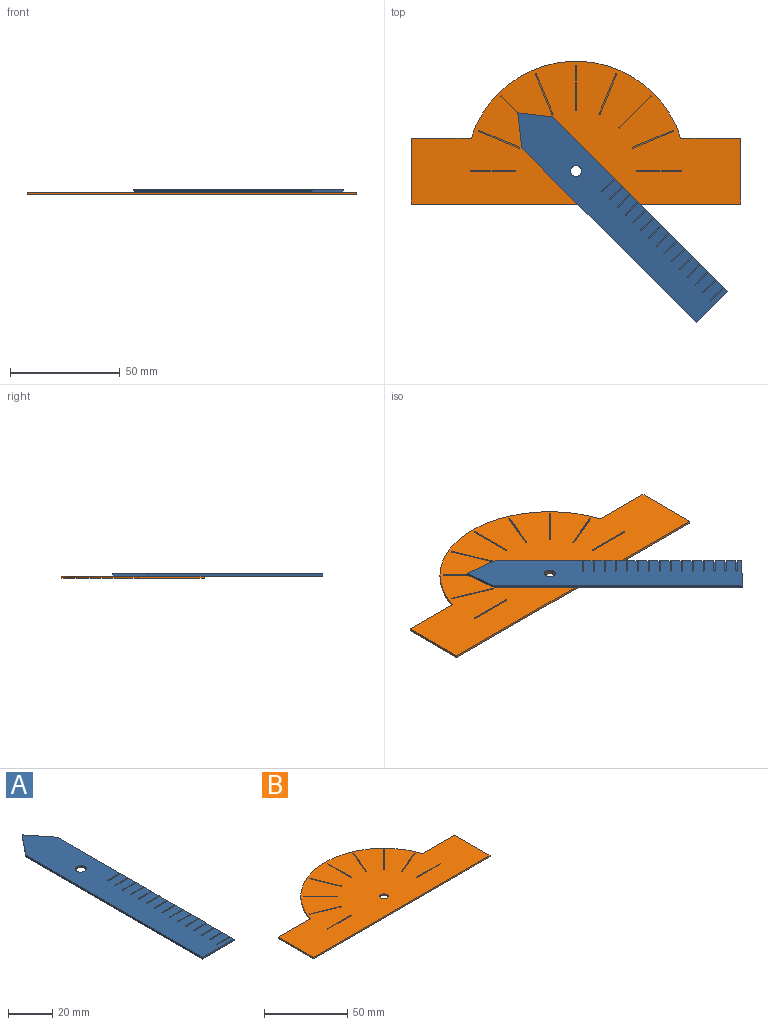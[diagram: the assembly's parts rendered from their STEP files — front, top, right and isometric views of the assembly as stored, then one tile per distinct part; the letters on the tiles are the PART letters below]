
ASSEMBLY  parts=2 mates=1
PART A: 68 faces, bbox 20x125x1 mm
  f0: plane 112.42x1mm, normal (1,0,0), area 108.7mm2, adj f1,f2,f5,f6,f8,f10,f11,f12
  f1: plane 125x20mm, normal (0,0,1), area 2293.1mm2, adj f0,f2,f3,f4,f5,f7,f8,f9
  f2: plane 12.58x10mm, normal (0.78,0.62,0), area 16.1mm2, adj f0,f1,f3,f6
  f3: plane 12.58x10mm, normal (-0.78,0.62,0), area 16.1mm2, adj f1,f2,f4,f6
  f4: plane 112.42x1mm, normal (-1,0,0), area 112.4mm2, adj f1,f3,f5,f6
  f5: plane 20x1mm, normal (0,-1,0), area 20mm2, adj f0,f1,f4,f6
  f6: plane 125x20mm, normal (0,0,-1), area 2354.5mm2, adj f0,f2,f3,f4,f5,f7
  f7: cylinder r=2.5mm len=5mm, axis (0,0,1), area 15.7mm2, adj f1,f6
  f8: plane 8x0.5mm, normal (0,-1,0), area 4mm2, adj f0,f1,f9,f11
  f9: cylinder r=0.25mm len=0.5mm, axis (0,0,1), area 0.4mm2, adj f1,f8,f10,f11
  f10: plane 8x0.5mm, normal (0,1,0), area 4mm2, adj f0,f1,f9,f11
  f11: plane 8.25x0.5mm, normal (0,0,1), area 4.1mm2, adj f0,f8,f9,f10
  f12: plane 8x0.5mm, normal (0,-1,0), area 4mm2, adj f0,f1,f13,f15
  f13: cylinder r=0.25mm len=0.5mm, axis (0,0,1), area 0.4mm2, adj f1,f12,f14,f15
  f14: plane 8x0.5mm, normal (0,1,0), area 4mm2, adj f0,f1,f13,f15
  f15: plane 8.25x0.5mm, normal (0,0,1), area 4.1mm2, adj f0,f12,f13,f14
  f16: plane 8x0.5mm, normal (0,-1,0), area 4mm2, adj f0,f1,f17,f19
  f17: cylinder r=0.25mm len=0.5mm, axis (0,0,1), area 0.4mm2, adj f1,f16,f18,f19
  f18: plane 8x0.5mm, normal (0,1,0), area 4mm2, adj f0,f1,f17,f19
  f19: plane 8.25x0.5mm, normal (0,0,1), area 4.1mm2, adj f0,f16,f17,f18
  f20: plane 8x0.5mm, normal (0,-1,0), area 4mm2, adj f0,f1,f21,f23
  f21: cylinder r=0.25mm len=0.5mm, axis (0,0,1), area 0.4mm2, adj f1,f20,f22,f23
  f22: plane 8x0.5mm, normal (0,1,0), area 4mm2, adj f0,f1,f21,f23
  f23: plane 8.25x0.5mm, normal (0,0,1), area 4.1mm2, adj f0,f20,f21,f22
  f24: plane 8x0.5mm, normal (0,-1,0), area 4mm2, adj f0,f1,f25,f27
  f25: cylinder r=0.25mm len=0.5mm, axis (0,0,1), area 0.4mm2, adj f1,f24,f26,f27
  f26: plane 8x0.5mm, normal (0,1,0), area 4mm2, adj f0,f1,f25,f27
  f27: plane 8.25x0.5mm, normal (0,0,1), area 4.1mm2, adj f0,f24,f25,f26
  f28: plane 8x0.5mm, normal (0,-1,0), area 4mm2, adj f0,f1,f29,f31
  f29: cylinder r=0.25mm len=0.5mm, axis (0,0,1), area 0.4mm2, adj f1,f28,f30,f31
  f30: plane 8x0.5mm, normal (0,1,0), area 4mm2, adj f0,f1,f29,f31
  f31: plane 8.25x0.5mm, normal (0,0,1), area 4.1mm2, adj f0,f28,f29,f30
  f32: plane 8x0.5mm, normal (0,-1,0), area 4mm2, adj f0,f1,f33,f35
  f33: cylinder r=0.25mm len=0.5mm, axis (0,0,1), area 0.4mm2, adj f1,f32,f34,f35
  f34: plane 8x0.5mm, normal (0,1,0), area 4mm2, adj f0,f1,f33,f35
  f35: plane 8.25x0.5mm, normal (0,0,1), area 4.1mm2, adj f0,f32,f33,f34
  f36: plane 8x0.5mm, normal (0,-1,0), area 4mm2, adj f0,f1,f37,f39
  f37: cylinder r=0.25mm len=0.5mm, axis (0,0,1), area 0.4mm2, adj f1,f36,f38,f39
  f38: plane 8x0.5mm, normal (0,1,0), area 4mm2, adj f0,f1,f37,f39
  f39: plane 8.25x0.5mm, normal (0,0,1), area 4.1mm2, adj f0,f36,f37,f38
  f40: plane 8x0.5mm, normal (0,-1,0), area 4mm2, adj f0,f1,f41,f43
  f41: cylinder r=0.25mm len=0.5mm, axis (0,0,1), area 0.4mm2, adj f1,f40,f42,f43
  f42: plane 8x0.5mm, normal (0,1,0), area 4mm2, adj f0,f1,f41,f43
  f43: plane 8.25x0.5mm, normal (0,0,1), area 4.1mm2, adj f0,f40,f41,f42
  f44: plane 8x0.5mm, normal (0,-1,0), area 4mm2, adj f0,f1,f45,f47
  f45: cylinder r=0.25mm len=0.5mm, axis (0,0,1), area 0.4mm2, adj f1,f44,f46,f47
  f46: plane 8x0.5mm, normal (0,1,0), area 4mm2, adj f0,f1,f45,f47
  f47: plane 8.25x0.5mm, normal (0,0,1), area 4.1mm2, adj f0,f44,f45,f46
  f48: plane 8x0.5mm, normal (0,-1,0), area 4mm2, adj f0,f1,f49,f51
  f49: cylinder r=0.25mm len=0.5mm, axis (0,0,1), area 0.4mm2, adj f1,f48,f50,f51
  f50: plane 8x0.5mm, normal (0,1,0), area 4mm2, adj f0,f1,f49,f51
  f51: plane 8.25x0.5mm, normal (0,0,1), area 4.1mm2, adj f0,f48,f49,f50
  f52: plane 8x0.5mm, normal (0,-1,0), area 4mm2, adj f0,f1,f53,f55
  f53: cylinder r=0.25mm len=0.5mm, axis (0,0,1), area 0.4mm2, adj f1,f52,f54,f55
  f54: plane 8x0.5mm, normal (0,1,0), area 4mm2, adj f0,f1,f53,f55
  f55: plane 8.25x0.5mm, normal (0,0,1), area 4.1mm2, adj f0,f52,f53,f54
  f56: plane 8x0.5mm, normal (0,-1,0), area 4mm2, adj f0,f1,f57,f59
  f57: cylinder r=0.25mm len=0.5mm, axis (0,0,1), area 0.4mm2, adj f1,f56,f58,f59
  f58: plane 8x0.5mm, normal (0,1,0), area 4mm2, adj f0,f1,f57,f59
  f59: plane 8.25x0.5mm, normal (0,0,1), area 4.1mm2, adj f0,f56,f57,f58
  f60: plane 8x0.5mm, normal (0,-1,0), area 4mm2, adj f0,f1,f61,f63
  f61: cylinder r=0.25mm len=0.5mm, axis (0,0,1), area 0.4mm2, adj f1,f60,f62,f63
  f62: plane 8x0.5mm, normal (0,1,0), area 4mm2, adj f0,f1,f61,f63
  f63: plane 8.25x0.5mm, normal (0,0,1), area 4.1mm2, adj f0,f60,f61,f62
  f64: plane 8x0.5mm, normal (0,1,0), area 4mm2, adj f0,f1,f66,f67
  f65: plane 8x0.5mm, normal (0,-1,0), area 4mm2, adj f0,f1,f66,f67
  f66: cylinder r=0.25mm len=0.5mm, axis (0,0,1), area 0.4mm2, adj f1,f64,f65,f67
  f67: plane 8.25x0.5mm, normal (0,0,1), area 4.1mm2, adj f0,f64,f65,f66
PART B: 54 faces, bbox 150x65x1 mm
  f0: plane 27.3x1mm, normal (0,1,0), area 27.3mm2, adj f1,f5,f6,f7
  f1: plane 30x1mm, normal (-1,0,0), area 30mm2, adj f0,f2,f6,f7
  f2: plane 150x1mm, normal (0,-1,0), area 150mm2, adj f1,f3,f6,f7
  f3: plane 30x1mm, normal (1,0,0), area 30mm2, adj f2,f4,f6,f7
  f4: plane 27.3x1mm, normal (0,1,0), area 27.3mm2, adj f3,f5,f6,f7
  f5: cylinder r=50mm len=95.39mm, axis (0,0,1), area 126.6mm2, adj f0,f4,f6,f7
  f6: plane 150x65mm, normal (0,0,-1), area 6930.2mm2, adj f0,f1,f2,f3,f4,f5,f8
  f7: plane 150x65mm, normal (0,0,1), area 6838.4mm2, adj f0,f1,f2,f3,f4,f5,f8,f9
  f8: cylinder r=2.5mm len=5mm, axis (0,0,1), area 15.7mm2, adj f6,f7
  f9: plane 20x0.5mm, normal (0,1,0), area 10mm2, adj f7,f10,f12,f13
  f10: cylinder r=0.25mm len=0.5mm, axis (0,0,1), area 0.4mm2, adj f7,f9,f11,f13
  f11: plane 20x0.5mm, normal (0,-1,0), area 10mm2, adj f7,f10,f12,f13
  f12: cylinder r=0.25mm len=0.5mm, axis (0,0,1), area 0.4mm2, adj f7,f9,f11,f13
  f13: plane 20.5x0.5mm, normal (0,0,1), area 10.2mm2, adj f9,f10,f11,f12
  f14: plane 18.48x7.65mm, normal (-0.38,0.92,0), area 10mm2, adj f7,f15,f17,f18
  f15: cylinder r=0.25mm len=0.5mm, axis (0,0,1), area 0.4mm2, adj f7,f14,f16,f18
  f16: plane 18.48x7.65mm, normal (0.38,-0.92,0), area 10mm2, adj f7,f15,f17,f18
  f17: cylinder r=0.25mm len=0.5mm, axis (0,0,1), area 0.4mm2, adj f7,f14,f16,f18
  f18: plane 18.98x8.15mm, normal (0,0,1), area 10.2mm2, adj f14,f15,f16,f17
  f19: plane 14.14x14.14mm, normal (-0.71,0.71,0), area 10mm2, adj f7,f20,f22,f23
  f20: cylinder r=0.25mm len=0.5mm, axis (0,0,1), area 0.4mm2, adj f7,f19,f21,f23
  f21: plane 14.14x14.14mm, normal (0.71,-0.71,0), area 10mm2, adj f7,f20,f22,f23
  f22: cylinder r=0.25mm len=0.5mm, axis (0,0,1), area 0.4mm2, adj f7,f19,f21,f23
  f23: plane 14.64x14.64mm, normal (0,0,1), area 10.2mm2, adj f19,f20,f21,f22
  f24: plane 18.48x7.65mm, normal (-0.92,0.38,0), area 10mm2, adj f7,f25,f27,f28
  f25: cylinder r=0.25mm len=0.5mm, axis (0,0,1), area 0.4mm2, adj f7,f24,f26,f28
  f26: plane 18.48x7.65mm, normal (0.92,-0.38,0), area 10mm2, adj f7,f25,f27,f28
  f27: cylinder r=0.25mm len=0.5mm, axis (0,0,1), area 0.4mm2, adj f7,f24,f26,f28
  f28: plane 18.98x8.15mm, normal (0,0,1), area 10.2mm2, adj f24,f25,f26,f27
  f29: plane 20x0.5mm, normal (-1,0,0), area 10mm2, adj f7,f30,f32,f33
  f30: cylinder r=0.25mm len=0.5mm, axis (0,0,1), area 0.4mm2, adj f7,f29,f31,f33
  f31: plane 20x0.5mm, normal (1,0,0), area 10mm2, adj f7,f30,f32,f33
  f32: cylinder r=0.25mm len=0.5mm, axis (0,0,1), area 0.4mm2, adj f7,f29,f31,f33
  f33: plane 20.5x0.5mm, normal (0,0,1), area 10.2mm2, adj f29,f30,f31,f32
  f34: plane 18.48x7.65mm, normal (-0.92,-0.38,0), area 10mm2, adj f7,f35,f37,f38
  f35: cylinder r=0.25mm len=0.5mm, axis (0,0,1), area 0.4mm2, adj f7,f34,f36,f38
  f36: plane 18.48x7.65mm, normal (0.92,0.38,0), area 10mm2, adj f7,f35,f37,f38
  f37: cylinder r=0.25mm len=0.5mm, axis (0,0,1), area 0.4mm2, adj f7,f34,f36,f38
  f38: plane 18.98x8.15mm, normal (0,0,1), area 10.2mm2, adj f34,f35,f36,f37
  f39: plane 14.14x14.14mm, normal (-0.71,-0.71,0), area 10mm2, adj f7,f40,f42,f43
  f40: cylinder r=0.25mm len=0.5mm, axis (0,0,1), area 0.4mm2, adj f7,f39,f41,f43
  f41: plane 14.14x14.14mm, normal (0.71,0.71,0), area 10mm2, adj f7,f40,f42,f43
  f42: cylinder r=0.25mm len=0.5mm, axis (0,0,1), area 0.4mm2, adj f7,f39,f41,f43
  f43: plane 14.64x14.64mm, normal (0,0,1), area 10.2mm2, adj f39,f40,f41,f42
  f44: plane 18.48x7.65mm, normal (-0.38,-0.92,0), area 10mm2, adj f7,f45,f47,f48
  f45: cylinder r=0.25mm len=0.5mm, axis (0,0,1), area 0.4mm2, adj f7,f44,f46,f48
  f46: plane 18.48x7.65mm, normal (0.38,0.92,0), area 10mm2, adj f7,f45,f47,f48
  f47: cylinder r=0.25mm len=0.5mm, axis (0,0,1), area 0.4mm2, adj f7,f44,f46,f48
  f48: plane 18.98x8.15mm, normal (0,0,1), area 10.2mm2, adj f44,f45,f46,f47
  f49: plane 20x0.5mm, normal (0,-1,0), area 10mm2, adj f7,f50,f52,f53
  f50: cylinder r=0.25mm len=0.5mm, axis (0,0,1), area 0.4mm2, adj f7,f49,f51,f53
  f51: plane 20x0.5mm, normal (0,1,0), area 10mm2, adj f7,f50,f52,f53
  f52: cylinder r=0.25mm len=0.5mm, axis (0,0,1), area 0.4mm2, adj f7,f49,f51,f53
  f53: plane 20.5x0.5mm, normal (0,0,1), area 10.2mm2, adj f49,f50,f51,f52
PLACE A rot(axis=(0,0,1),45deg) t=(0,0,0)mm
PLACE B at identity fixed
MATE revolute B.f8 <-> A.f7  axis (0,0,1) through (0,0,-0.5)mm
